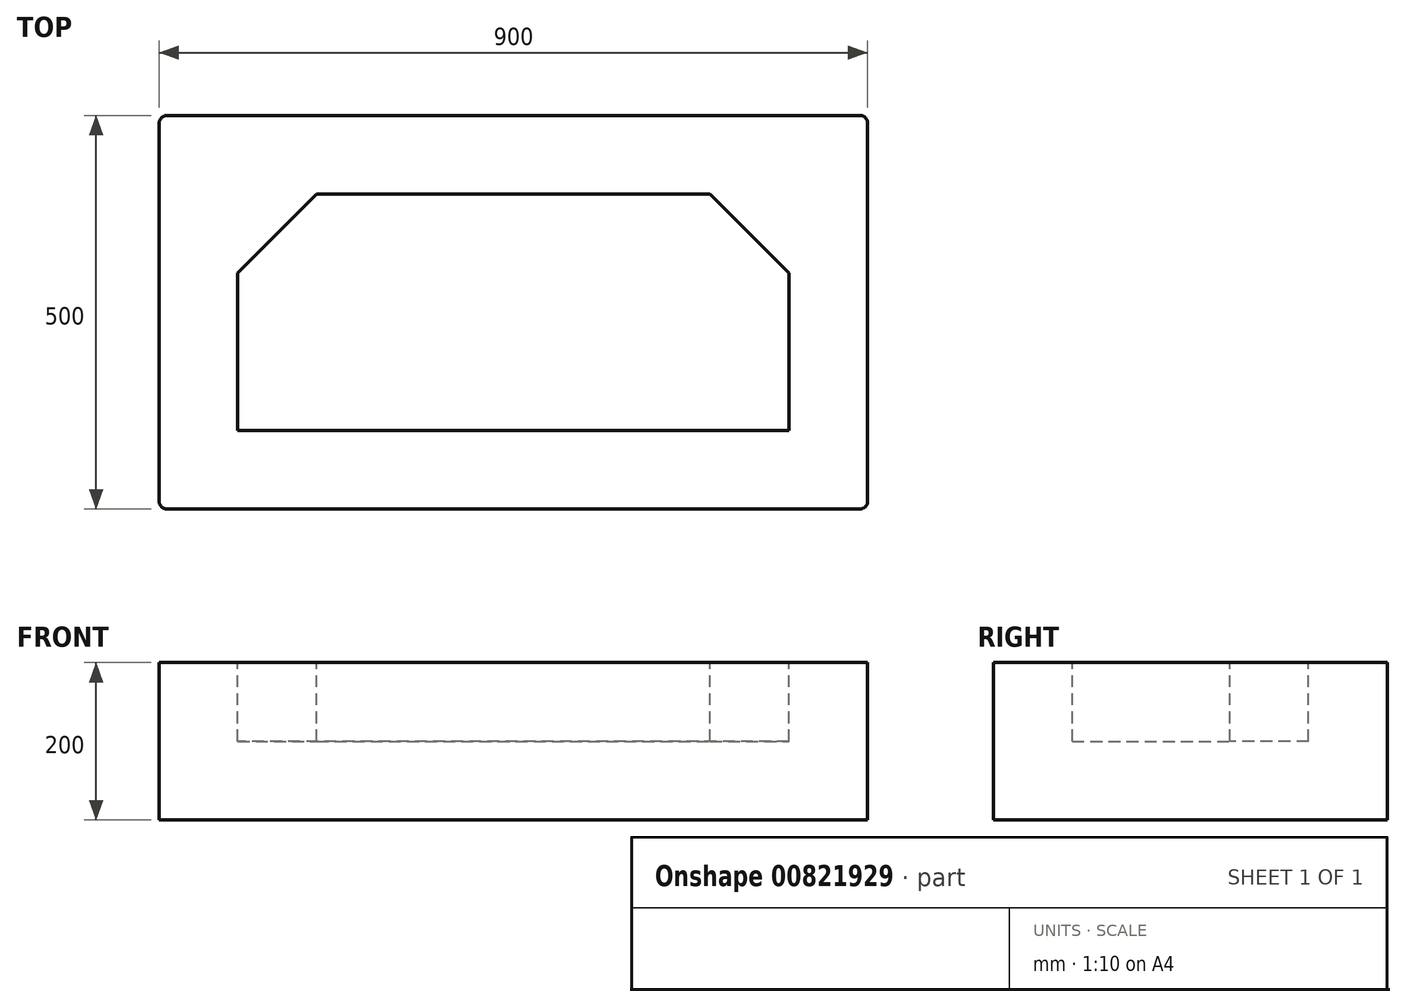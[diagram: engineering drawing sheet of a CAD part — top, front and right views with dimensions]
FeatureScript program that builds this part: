
annotation { "Feature Type Name" : "Feature", "Feature Type Description" : "" }
export const myFeature = defineFeature(function(context is Context, id is Id, definition is map)
    precondition{}
    {
        {
            var Q0;
            Q0=qCreatedBy(makeId("Front.planeOp"),FACE);
            var sketch = newSketch(context, id + "F0", { "sketchPlane" : qUnion([Q0])});
            skLineSegment(sketch, "E0.bottom", {"start": v(450, 100) * mm, "end": v(-450, 100) * mm});
            skLineSegment(sketch, "E0.top", {"start": v(450, -100) * mm, "end": v(-450, -100) * mm});
            skLineSegment(sketch, "E0.left", {"start": v(450, 100) * mm, "end": v(450, -100) * mm});
            skLineSegment(sketch, "E0.right", {"start": v(-450, 100) * mm, "end": v(-450, -100) * mm});
            skPoint(sketch, "E0.middle", {"position": v(0, 0) * mm});
            skSolve(sketch);
        }
        {
            var Q0;
            Q0=makeQuery(id+"F0.imprint","IMPRINT",FACE,{"disambiguationData":[TD([[makeQuery(id+"F0.imprint","IMPRINT",EDGE,{"derivedFrom":sQuery(id+"F0.wireOp",EDGE,"E0.bottom")}),1.0]])]});
            extrude(context, id + "F1", {"entities" : qUnion([Q0]), "endBound" : BoundingType.SYMMETRIC, "depth" : 500 * mm, "offsetDistance" : 25 * mm});
        }
        {
            var Q0;
            Q0=makeQuery(id+"F1.opExtrude","SWEPT_FACE",FACE,{"disambiguationData":[OSD([sQuery(id+"F0.wireOp",EDGE,"E0.bottom")])]});
            var sketch = newSketch(context, id + "F2", { "sketchPlane" : qUnion([Q0])});
            skLineSegment(sketch, "E1.bottom", {"start": v(350, -150) * mm, "end": v(-350, -150) * mm});
            skPoint(sketch, "E1.middle", {"position": v(0, 0) * mm});
            skLineSegment(sketch, "E2", {"start": v(-350, -150) * mm, "end": v(-350, 50) * mm});
            skLineSegment(sketch, "E3", {"start": v(0, 150) * mm, "end": v(-250, 150) * mm});
            skLineSegment(sketch, "E4", {"start": v(-350, 50) * mm, "end": v(-250, 150) * mm});
            skLineSegment(sketch, "E5", {"start": v(0, 150) * mm, "end": v(250, 150) * mm});
            skLineSegment(sketch, "E6", {"start": v(350, -150) * mm, "end": v(350, 50) * mm});
            skLineSegment(sketch, "E7", {"start": v(250, 150) * mm, "end": v(350, 50) * mm});
            skSolve(sketch);
        }
        {
            var Q0;
            Q0 = qSketchRegion(id + "F2", true);
            extrude(context, id + "F3", {"entities" : qUnion([Q0]), "operationType" : NewBodyOperationType.REMOVE, "oppositeDirection" : true, "depth" : 100 * mm, "offsetDistance" : 25 * mm});
        }
        {
            var Q0;
            Q0=makeQuery(id+"F1.opExtrude","CAP_EDGE",EDGE,{"disambiguationData":[OSD([sQuery(id+"F0.wireOp",EDGE,"E0.left")])],"isStart":false});
            var Q1;
            Q1=makeQuery(id+"F1.opExtrude","CAP_EDGE",EDGE,{"disambiguationData":[OSD([sQuery(id+"F0.wireOp",EDGE,"E0.right")])],"isStart":false});
            var Q2;
            Q2=makeQuery(id+"F1.opExtrude","CAP_EDGE",EDGE,{"disambiguationData":[OSD([sQuery(id+"F0.wireOp",EDGE,"E0.left")])],"isStart":true});
            var Q3;
            Q3=makeQuery(id+"F1.opExtrude","CAP_EDGE",EDGE,{"disambiguationData":[OSD([sQuery(id+"F0.wireOp",EDGE,"E0.right")])],"isStart":true});
            fillet(context, id + "F4", {"entities" : qUnion([Q0, Q1, Q2, Q3]), "radius" : 10 * mm, "tangentPropagation" : true, "allowEdgeOverflow" : false});
        }
    });
